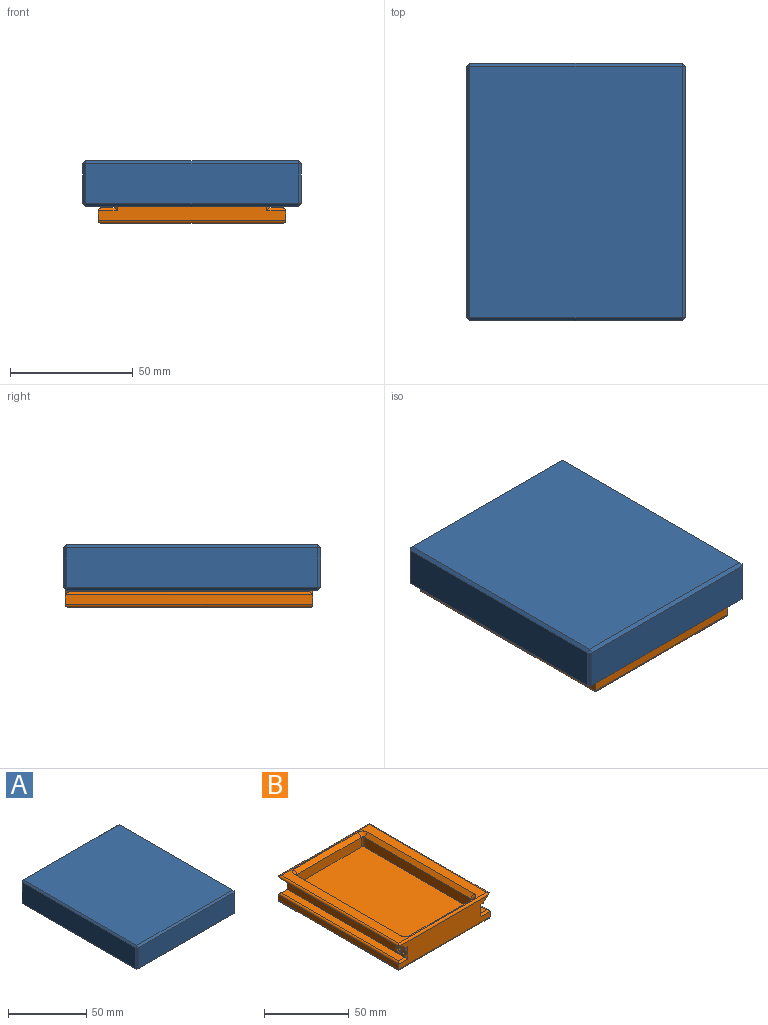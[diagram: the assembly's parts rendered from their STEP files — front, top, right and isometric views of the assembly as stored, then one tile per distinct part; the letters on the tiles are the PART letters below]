
ASSEMBLY  parts=2 mates=1
PART A: 68 faces, bbox 89x104.9x19.7 mm
  f0: plane 4.82x3.3mm, normal (1,0,0), area 13.9mm2, adj f15,f20,f22,f23
  f1: plane 4.82x3.3mm, normal (-1,0,0), area 13.9mm2, adj f15,f19,f51,f67
  f2: plane 92.45x3.3mm, normal (1,0,0), area 303.3mm2, adj f20,f26,f27,f28
  f3: plane 3.19x0.19mm, normal (0,0,1), area 0.1mm2, adj f4,f25
  f4: plane 100.33x5.08mm, normal (0.69,0,0.72), area 703mm2, adj f3,f5,f15,f23,f28,f35
  f5: plane 100.33x1.78mm, normal (1,0,0), area 178.4mm2, adj f4,f6,f15,f41
  f6: plane 100.33x76.71mm, normal (0,0,-1), area 7696.1mm2, adj f5,f7,f15,f45
  f7: plane 100.33x1.78mm, normal (-1,0,0), area 178.4mm2, adj f6,f8,f15,f50
  f8: plane 100.33x5.08mm, normal (-0.69,0,0.72), area 703mm2, adj f7,f9,f15,f51,f54,f59
  f9: plane 3.19x0.19mm, normal (0,0,1), area 0.1mm2, adj f8,f55
  f10: plane 92.45x3.3mm, normal (-1,0,0), area 303.3mm2, adj f19,f59,f63,f65
  f11: plane 102.37x86.49mm, normal (0,0,-1), area 2152.9mm2, adj f15,f22,f24,f26,f31,f36,f46,f56
  f12: plane 102.24x16.26mm, normal (1,0,0), area 1661.9mm2, adj f47,f48,f56,f57
  f13: plane 102.24x86.36mm, normal (0,0,1), area 8829mm2, adj f38,f39,f48,f49
  f14: plane 102.24x16.26mm, normal (-1,0,0), area 1661.9mm2, adj f36,f37,f39,f40
  f15: plane 76.71x12.45mm, normal (0,1,0), area 859.2mm2, adj f0,f1,f4,f5,f6,f7,f8,f11
  f16: plane 86.36x16.26mm, normal (0,-1,0), area 1403.9mm2, adj f37,f38,f46,f47
  f17: sphere r=1.4mm, area 6.7mm2, adj f20
  f18: sphere r=1.4mm, area 6.1mm2, adj f19
  f19: torus R=2.35mm, axis (-1,0,0), area 13mm2, adj f1,f10,f18,f55,f66
  f20: torus R=2.35mm, axis (-1,0,0), area 13.2mm2, adj f0,f2,f17,f24,f25
  f21: plane 86.36x16.26mm, normal (0,1,0), area 491.9mm2, adj f27,f31,f33,f35,f40,f41,f45,f49
  f22: plane 4.57x1.27mm, normal (0.71,0,-0.71), area 8.2mm2, adj f0,f11,f15,f24
  f23: plane 4.82x1.27mm, normal (0.71,0,0.71), area 8.7mm2, adj f0,f4,f15,f25
  f24: bspline ~3.57x1.34mm, area 5.8mm2, adj f11,f20,f22,f26
  f25: bspline ~3.06x1.3mm, area 5.1mm2, adj f3,f20,f23,f28
  f26: plane 92.2x1.27mm, normal (0.71,0,-0.71), area 165.6mm2, adj f2,f11,f24,f29
  f27: plane 3.3x1.27mm, normal (0.71,0.71,0), area 5.9mm2, adj f2,f21,f29,f30
  f28: plane 92.45x1.27mm, normal (0.71,0,0.71), area 166mm2, adj f2,f4,f25,f30
  f29: plane 1.27x1.27mm, normal (0.58,0.58,-0.58), area 1.4mm2, adj f26,f27,f31
  f30: plane 1.27x1.27mm, normal (0.58,0.58,0.58), area 1.4mm2, adj f27,f28,f33
  f31: plane 9.91x1.27mm, normal (0,0.71,-0.71), area 17.8mm2, adj f11,f21,f29,f34
  f32: plane 1.27x1.27mm, normal (-0.58,-0.58,0.58), area 1.4mm2, adj f37,f38,f39
  f33: plane 1.27x1.27mm, normal (0,0.71,0.71), area 0.5mm2, adj f21,f30,f35
  f34: plane 1.27x1.27mm, normal (-0.58,0.58,-0.58), area 1.4mm2, adj f31,f36,f40
  f35: plane 6.35x6.1mm, normal (0.49,0.71,0.51), area 13.5mm2, adj f4,f21,f33,f41
  f36: plane 102.24x1.27mm, normal (-0.71,0,-0.71), area 183.6mm2, adj f11,f14,f34,f42
  f37: plane 16.26x1.27mm, normal (-0.71,-0.71,0), area 29.2mm2, adj f14,f16,f32,f42
  f38: plane 86.36x1.27mm, normal (0,-0.71,0.71), area 155.1mm2, adj f13,f16,f32,f43
  f39: plane 102.24x1.27mm, normal (-0.71,0,0.71), area 183.6mm2, adj f13,f14,f32,f44
  f40: plane 16.26x1.27mm, normal (-0.71,0.71,0), area 29.2mm2, adj f14,f21,f34,f44
  f41: plane 3.59x1.27mm, normal (0.71,0.71,0), area 4.8mm2, adj f5,f21,f35,f45
  f42: plane 1.27x1.27mm, normal (-0.58,-0.58,-0.58), area 1.4mm2, adj f36,f37,f46
  f43: plane 1.27x1.27mm, normal (0.58,-0.58,0.58), area 1.4mm2, adj f38,f47,f48
  f44: plane 1.27x1.27mm, normal (-0.58,0.58,0.58), area 1.4mm2, adj f39,f40,f49
  f45: plane 79.25x1.27mm, normal (0,0.71,-0.71), area 140.1mm2, adj f6,f21,f41,f50
  f46: plane 86.36x1.27mm, normal (0,-0.71,-0.71), area 155.1mm2, adj f11,f16,f42,f52
  f47: plane 16.26x1.27mm, normal (0.71,-0.71,0), area 29.2mm2, adj f12,f16,f43,f52
  f48: plane 102.24x1.27mm, normal (0.71,0,0.71), area 183.6mm2, adj f12,f13,f43,f53
  f49: plane 86.36x1.27mm, normal (0,0.71,0.71), area 155.1mm2, adj f13,f21,f44,f53
  f50: plane 3.59x1.27mm, normal (-0.71,0.71,0), area 4.8mm2, adj f7,f21,f45,f54
  f51: plane 4.82x1.27mm, normal (-0.71,0,0.71), area 8.7mm2, adj f1,f8,f15,f55
  f52: plane 1.27x1.27mm, normal (0.58,-0.58,-0.58), area 1.4mm2, adj f46,f47,f56
  f53: plane 1.27x1.27mm, normal (0.58,0.58,0.58), area 1.4mm2, adj f48,f49,f57
  f54: plane 6.35x6.1mm, normal (-0.49,0.71,0.51), area 13.5mm2, adj f8,f21,f50,f58
  f55: bspline ~3.06x1.3mm, area 5.1mm2, adj f9,f19,f51,f59
  f56: plane 102.24x1.27mm, normal (0.71,0,-0.71), area 183.6mm2, adj f11,f12,f52,f60
  f57: plane 16.26x1.27mm, normal (0.71,0.71,0), area 29.2mm2, adj f12,f21,f53,f60
  f58: plane 1.27x1.27mm, normal (0,0.71,0.71), area 0.5mm2, adj f21,f54,f61
  f59: plane 92.45x1.27mm, normal (-0.71,0,0.71), area 166mm2, adj f8,f10,f55,f61
  f60: plane 1.27x1.27mm, normal (0.58,0.58,-0.58), area 1.4mm2, adj f56,f57,f62
  f61: plane 1.27x1.27mm, normal (-0.58,0.58,0.58), area 1.4mm2, adj f58,f59,f63
  f62: plane 9.91x1.27mm, normal (0,0.71,-0.71), area 17.8mm2, adj f11,f21,f60,f64
  f63: plane 3.3x1.27mm, normal (-0.71,0.71,0), area 5.9mm2, adj f10,f21,f61,f64
  f64: plane 1.27x1.27mm, normal (-0.58,0.58,-0.58), area 1.4mm2, adj f62,f63,f65
  f65: plane 92.2x1.27mm, normal (-0.71,0,-0.71), area 165.6mm2, adj f10,f11,f64,f66
  f66: bspline ~3.57x1.34mm, area 5.8mm2, adj f11,f19,f65,f67
  f67: plane 4.57x1.27mm, normal (-0.71,0,-0.71), area 8.2mm2, adj f1,f11,f15,f66
PART B: 68 faces, bbox 76.2x100.8x19.1 mm
  f0: plane 98.3x6.35mm, normal (1,0,0), area 596.9mm2, adj f1,f2,f3,f11,f12,f43,f63,f64
  f1: plane 8.89x1.27mm, normal (0.71,-0.71,0), area 11.4mm2, adj f0,f15,f40,f41,f63,f64,f65
  f2: torus R=2.56mm, axis (-1,0,0), area 12.4mm2, adj f0,f3,f50,f64,f65
  f3: torus R=2.56mm, axis (-1,0,0), area 0.9mm2, adj f0,f2,f63
  f4: plane 98.3x6.35mm, normal (-1,0,0), area 596.9mm2, adj f5,f13,f14,f47,f51,f60,f61
  f5: plane 8.89x1.27mm, normal (-0.71,-0.71,0), area 10.9mm2, adj f4,f15,f36,f37,f60,f61,f62
  f6: sphere r=1.59mm, area 8.6mm2, adj f51,f60,f61,f62
  f7: plane 98.3x73.66mm, normal (0,0,1), area 1377mm2, adj f32,f33,f34,f35,f52,f53,f54,f55
  f8: plane 100.84x3.81mm, normal (-1,0,0), area 384.2mm2, adj f15,f16,f31,f67
  f9: plane 98.3x73.66mm, normal (0,0,-1), area 7240.6mm2, adj f28,f29,f30,f31
  f10: plane 100.84x3.81mm, normal (1,0,0), area 384.2mm2, adj f15,f16,f28,f66
  f11: plane 98.3x5.08mm, normal (0,0,1), area 499.4mm2, adj f0,f41,f42,f66
  f12: plane 98.3x1.27mm, normal (0,0,-1), area 124.8mm2, adj f0,f27,f40,f44
  f13: plane 98.3x1.27mm, normal (0,0,-1), area 124.8mm2, adj f4,f26,f37,f48
  f14: plane 98.3x5.08mm, normal (0,0,1), area 499.4mm2, adj f4,f36,f46,f67
  f15: plane 76.2x16.51mm, normal (0,-1,0), area 1094.4mm2, adj f1,f5,f8,f10,f29,f33,f36,f37
  f16: plane 76.2x16.51mm, normal (0,1,0), area 1094.4mm2, adj f8,f10,f30,f34,f42,f43,f44,f45
  f17: plane 88.77x6.99mm, normal (1,0,0), area 620.1mm2, adj f21,f22,f25,f55
  f18: plane 53.34x6.99mm, normal (0,1,0), area 372.6mm2, adj f21,f22,f23,f52
  f19: plane 88.77x6.99mm, normal (-1,0,0), area 620.1mm2, adj f21,f23,f24,f56
  f20: plane 53.34x6.99mm, normal (0,-1,0), area 372.6mm2, adj f21,f24,f25,f59
  f21: plane 91.31x55.88mm, normal (0,0,1), area 5101.2mm2, adj f17,f18,f19,f20,f22,f23,f24,f25
  f22: cylinder r=1.27mm len=6.99mm, axis (0,0,1), area 13.9mm2, adj f17,f18,f21,f53
  f23: cylinder r=1.27mm len=6.99mm, axis (0,0,-1), area 13.9mm2, adj f18,f19,f21,f54
  f24: cylinder r=1.27mm len=6.99mm, axis (0,0,1), area 13.9mm2, adj f19,f20,f21,f58
  f25: cylinder r=1.27mm len=6.99mm, axis (0,0,-1), area 13.9mm2, adj f17,f20,f21,f57
  f26: plane 98.3x5.08mm, normal (-0.71,0,-0.71), area 706.2mm2, adj f13,f32,f38,f49
  f27: plane 98.3x5.08mm, normal (0.71,0,-0.71), area 706.2mm2, adj f12,f35,f39,f45
  f28: cylinder r=1.27mm len=100.84mm, axis (0,1,0), area 199.3mm2, adj f9,f10,f29,f30
  f29: cylinder r=1.27mm len=76.2mm, axis (-1,0,0), area 150.2mm2, adj f9,f15,f28,f31
  f30: cylinder r=1.27mm len=76.2mm, axis (1,0,0), area 150.2mm2, adj f9,f16,f28,f31
  f31: cylinder r=1.27mm len=100.84mm, axis (0,-1,0), area 199.3mm2, adj f8,f9,f29,f30
  f32: cylinder r=1.27mm len=100.09mm, axis (0,1,0), area 197.9mm2, adj f7,f26,f33,f34,f38,f49
  f33: cylinder r=1.27mm len=75.46mm, axis (1,0,0), area 148.1mm2, adj f7,f15,f32,f35,f38,f39
  f34: cylinder r=1.27mm len=75.46mm, axis (-1,0,0), area 148.1mm2, adj f7,f16,f32,f35,f45,f49
  f35: cylinder r=1.27mm len=100.09mm, axis (0,-1,0), area 197.9mm2, adj f7,f27,f33,f34,f39,f45
  f36: plane 7.62x1.27mm, normal (0,-0.71,0.71), area 12.1mm2, adj f5,f14,f15,f67
  f37: plane 2.54x1.27mm, normal (0,-0.71,-0.71), area 2.9mm2, adj f5,f13,f15,f38
  f38: plane 5.98x5.61mm, normal (-0.5,-0.71,-0.5), area 12.6mm2, adj f15,f26,f32,f33,f37
  f39: plane 5.98x5.61mm, normal (0.5,-0.71,-0.5), area 12.6mm2, adj f15,f27,f33,f35,f40
  f40: plane 2.54x1.27mm, normal (0,-0.71,-0.71), area 2.9mm2, adj f1,f12,f15,f39
  f41: plane 7.62x1.27mm, normal (0,-0.71,0.71), area 12.1mm2, adj f1,f11,f15,f66
  f42: plane 7.62x1.27mm, normal (0,0.71,0.71), area 12.1mm2, adj f11,f16,f43,f66
  f43: plane 8.89x1.27mm, normal (0.71,0.71,0), area 13.7mm2, adj f0,f16,f42,f44
  f44: plane 2.54x1.27mm, normal (0,0.71,-0.71), area 2.9mm2, adj f12,f16,f43,f45
  f45: plane 5.98x5.61mm, normal (0.5,0.71,-0.5), area 12.6mm2, adj f16,f27,f34,f35,f44
  f46: plane 7.62x1.27mm, normal (0,0.71,0.71), area 12.1mm2, adj f14,f16,f47,f67
  f47: plane 8.89x1.27mm, normal (-0.71,0.71,0), area 13.7mm2, adj f4,f16,f46,f48
  f48: plane 2.54x1.27mm, normal (0,0.71,-0.71), area 2.9mm2, adj f13,f16,f47,f49
  f49: plane 5.98x5.61mm, normal (-0.5,0.71,-0.5), area 12.6mm2, adj f16,f26,f32,f34,f48
  f50: sphere r=1.59mm, area 8.8mm2, adj f2
  f51: torus R=2.56mm, axis (-1,0,0), area 13.1mm2, adj f4,f6,f60,f61
  f52: plane 53.34x2.54mm, normal (0,0.71,0.71), area 191.6mm2, adj f7,f18,f53,f54
  f53: cone r=3.81mm half-angle=45deg, axis (0,0,1), area 14.3mm2, adj f7,f22,f52,f55
  f54: cone r=3.81mm half-angle=45deg, axis (0,0,1), area 14.3mm2, adj f7,f23,f52,f56
  f55: plane 88.77x2.54mm, normal (0.71,0,0.71), area 318.9mm2, adj f7,f17,f53,f57
  f56: plane 88.77x2.54mm, normal (-0.71,0,0.71), area 318.9mm2, adj f7,f19,f54,f58
  f57: cone r=3.81mm half-angle=45deg, axis (0,0,1), area 14.3mm2, adj f7,f25,f55,f59
  f58: cone r=3.81mm half-angle=45deg, axis (0,0,1), area 14.3mm2, adj f7,f24,f56,f59
  f59: plane 53.34x2.54mm, normal (0,-0.71,0.71), area 191.6mm2, adj f7,f20,f57,f58
  f60: plane 5.27x0.76mm, normal (0,0,-1), area 3.3mm2, adj f4,f5,f6,f51,f62
  f61: plane 5.27x0.76mm, normal (0,0,1), area 3.3mm2, adj f4,f5,f6,f51,f62
  f62: plane 5.27x2.54mm, normal (-1,0,0), area 11.9mm2, adj f5,f6,f60,f61
  f63: plane 5x0.64mm, normal (0,0,-1), area 2.7mm2, adj f0,f1,f3,f65
  f64: plane 5x0.64mm, normal (0,0,1), area 2.7mm2, adj f0,f1,f2,f65
  f65: plane 5x2.54mm, normal (1,0,0), area 11.4mm2, adj f1,f2,f63,f64
  f66: cylinder r=1.27mm len=100.84mm, axis (0,1,0), area 197.9mm2, adj f10,f11,f41,f42
  f67: cylinder r=1.27mm len=100.84mm, axis (0,1,0), area 197.9mm2, adj f8,f14,f36,f46
PLACE A t=(-2.65,49.65,6.93)mm fixed
PLACE B t=(3.7,55.23,0.18)mm
MATE planar B.f15 <-> A.f15  axis (0,-1,0) through (41.8,-45.6,9.55)mm
